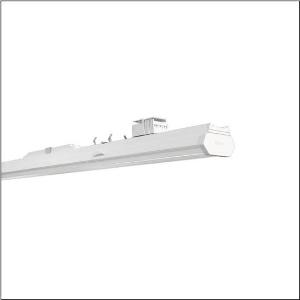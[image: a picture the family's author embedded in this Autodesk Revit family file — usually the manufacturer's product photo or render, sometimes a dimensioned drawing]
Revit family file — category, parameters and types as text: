
# Revit family: licross_r__11_protected_ho_51tp12mn4f5m_a747
name_source: partatom
category: Lighting Fixtures
units: mm (PartAtom-declared; Revit-internal decimal feet)

## family parameters
Cut with Voids When Loaded = No
Host = Face
Light Source = No
Part Type = Normal
Room Calculation Point = No
Round Connector Dimension = Use Diameter
Shared = No

## types (1)
- --- (1 x LED, 15820 lm, 87.4 W, 4000K)
    Apparent Load = 87 VA
    CIE Flux Codes = 70 91 97 98 100
    Color Rendering = 80
    Color Temperature = 4000K
    Default Elevation = 1800 mm
    Description = Licross® 11 Protected HO, luminaire insert, of sheet steel, galvanised, coil coated, white, length: 1.500mm, width: 90mm, height: 101mm, LED rated luminous flux: 15.820lm, light colour: 840, control gear: ON/OFF Multilumen, with plug, 3-pole, with phase selection, mains connection: 220..240V, AC, 50/60Hz, rated input power: 87W, halogen-free wiring, primary light control with lens, of plastic, primary optical cover: cover, of PMMA, light emission: direct distribution, primary light characteristic: symmetric, protection rating (complete): IP64, insulation class (complete): insulation class I (protective earthing), certification: CE, ENEC, VDE, UKCA, protection symbol: D if used in an environment with conductive dust loads with corresponding accessories, impact resistance: IK06, permissible ambient temperature for indoor applications: -35..+35°C, corresponds to IFS (International Featured Standards) requirements for safety and quality in the food industry, reducing of maximum allowable ambient temperature of 5°C with ceiling mounting, LABS conformity tested according to VDMA 24364:2018-05, packaging unit: 1 piece
    Height = 92 mm
    Lamp = 1 x LED
    Lamp Light Flux = 15820 lm
    Lamp Power = 87.4 W
    Lamp count = 1
    Length = 1500 mm
    Luminous efficacy = 181 lm/W
    Manufacturer = Siteco
    ModVariant = No
    Model = 51TP12MN4F5M
    Mounting Place = Ceiling
    Mounting Type = Pendant
    Number of Poles = 1
    OnlyDefault = Yes
    Power Factor = 1
    Product Name = Licross® 11 Protected HO
    Product group = luminaire insert
    ProductGroupID = 901
    Protection Class = Protection class I
    Protection Degree = IP 64
    RLX_Detail_Level = 1
    RLX_Emergency_Light_Flux = 0 lm
    RLX_Emergency_Type = 0
    RLX_Emergency_Type_DB = No
    RlxData = <blob elided: 22097 chars, md5=9570493e>
    Socket = socket
    Standby Power = 0 W
    System Light Flux = 15820 lm
    System Power = 87 W
    Type Comments = factory setting: luminous flux: 100 % | (A | C | E) | 203 mA
    Type Image = l_1256148.jpg
    URL = http://relux.com
    VarID = @adj_038173
    Voltage = 0 V
    Weight = 0.00 kg
    Width = 88 mm

## geometry (parser evidence)
native form markers: Blend x4, Sweep x9
no freeform markers — native parametric forms only
